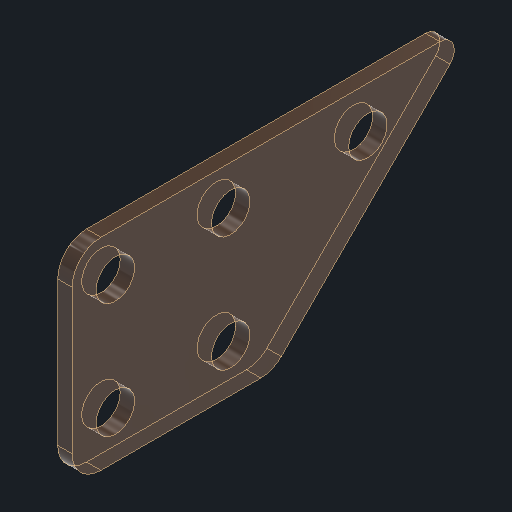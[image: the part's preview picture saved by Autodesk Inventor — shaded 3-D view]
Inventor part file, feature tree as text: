
AUTODESK INVENTOR PART (.ipt)
format: ipt  version: 2024 (Build 280153000, 153)  size: 127,488 bytes
history: native  units: in
note: dims shown in document units (in); Inventor stores cm internally (conversion verified against a paired STEP export)
features: other x3, sketch x2
ambient origin geometry x8: Origin, YZ Plane, XZ Plane, XY Plane, X Axis, Y Axis, Z Axis, Center Point
bodies: Solid1 (feature_tree)
feature tree (5):
  other  "sled.ipt"
  other  "Solid1::sled.ipt"
  other  "TaggingFeature1"
  sketch  "Sketch1"  dims[d0=0.3937in]
  sketch  "Sketch2"
